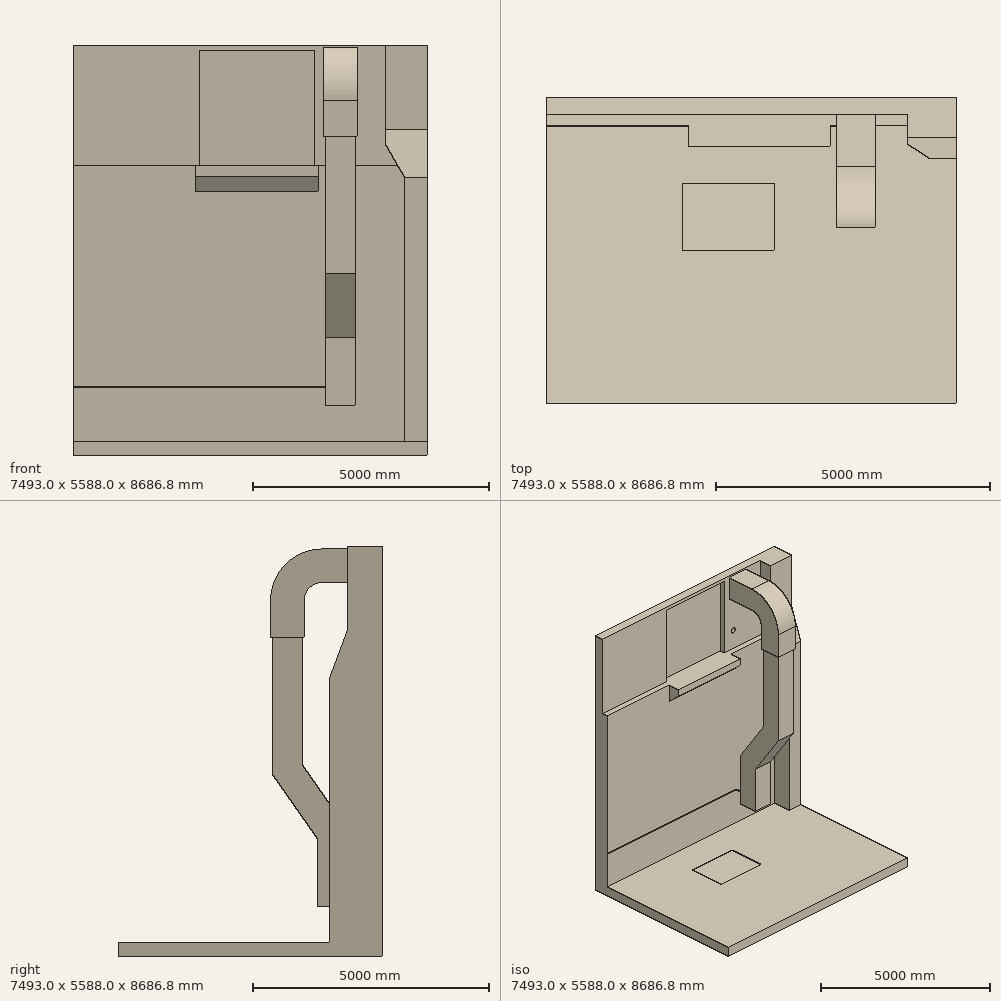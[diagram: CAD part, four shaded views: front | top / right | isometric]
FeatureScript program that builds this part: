
annotation { "Feature Type Name" : "Feature", "Feature Type Description" : "" }
export const myFeature = defineFeature(function(context is Context, id is Id, definition is map)
    precondition{}
    {
        {
            var Q0;
            Q0=qCreatedBy(makeId("Front.planeOp"),FACE);
            var sketch = newSketch(context, id + "F0", { "sketchPlane" : qUnion([Q0])});
            skLineSegment(sketch, "E0", {"start": v(0, 0) * mm, "end": v(0, 6146.8) * mm});
            skLineSegment(sketch, "E1", {"start": v(0, 6146.8) * mm, "end": v(7493, 6146.8) * mm});
            skLineSegment(sketch, "E2", {"start": v(7493, 6146.8) * mm, "end": v(7493, 0) * mm});
            skLineSegment(sketch, "E3", {"start": v(7493, 0) * mm, "end": v(0, 0) * mm});
            skSolve(sketch);
        }
        {
            var Q0;
            Q0=makeQuery(id+"F0.imprint","IMPRINT",FACE,{"disambiguationData":[TD([[makeQuery(id+"F0.imprint","IMPRINT",EDGE,{"derivedFrom":sQuery(id+"F0.wireOp",EDGE,"E0")}),-1.0]])]});
            extrude(context, id + "F1", {"entities" : qUnion([Q0]), "depth" : 508 * mm});
        }
        {
            var Q0;
            Q0=makeQuery(id+"F1.opExtrude","CAP_FACE",FACE,{"disambiguationData":[OSD([sQuery(id+"F0.wireOp",EDGE,"E0"),sQuery(id+"F0.wireOp",EDGE,"E1"),sQuery(id+"F0.wireOp",EDGE,"E2"),sQuery(id+"F0.wireOp",EDGE,"E3")])],"isStart":false});
            var sketch = newSketch(context, id + "F2", { "sketchPlane" : qUnion([Q0])});
            skLineSegment(sketch, "E4.bottom", {"start": v(0, 0) * mm, "end": v(7493, 0) * mm});
            skLineSegment(sketch, "E4.top", {"start": v(0, 304.8) * mm, "end": v(7493, 304.8) * mm});
            skLineSegment(sketch, "E4.left", {"start": v(0, 0) * mm, "end": v(0, 304.8) * mm});
            skLineSegment(sketch, "E4.right", {"start": v(7493, 0) * mm, "end": v(7493, 304.8) * mm});
            skSolve(sketch);
        }
        {
            var Q0;
            Q0=makeQuery(id+"F2.imprint","IMPRINT",FACE,{"disambiguationData":[TD([[makeQuery(id+"F2.imprint","IMPRINT",EDGE,{"derivedFrom":sQuery(id+"F2.wireOp",EDGE,"E4.bottom")}),-1.0]])]});
            extrude(context, id + "F3", {"entities" : qUnion([Q0]), "operationType" : NewBodyOperationType.ADD, "depth" : 5080 * mm});
        }
        {
            var Q0;
            Q0=makeQuery(id+"F1.opExtrude","SWEPT_FACE",FACE,{"disambiguationData":[OSD([sQuery(id+"F0.wireOp",EDGE,"E1")])]});
            var sketch = newSketch(context, id + "F4", { "sketchPlane" : qUnion([Q0])});
            skLineSegment(sketch, "E5.bottom", {"start": v(0, 0) * mm, "end": v(7493, 0) * mm});
            skLineSegment(sketch, "E5.top", {"start": v(0, -304.8) * mm, "end": v(7493, -304.8) * mm});
            skLineSegment(sketch, "E5.left", {"start": v(0, 0) * mm, "end": v(0, -304.8) * mm});
            skLineSegment(sketch, "E5.right", {"start": v(7493, 0) * mm, "end": v(7493, -304.8) * mm});
            skSolve(sketch);
        }
        {
            var Q0;
            Q0=makeQuery(id+"F4.imprint","IMPRINT",FACE,{"disambiguationData":[TD([[makeQuery(id+"F4.imprint","IMPRINT",EDGE,{"derivedFrom":sQuery(id+"F4.wireOp",EDGE,"E5.bottom")}),-1.0]])]});
            extrude(context, id + "F5", {"entities" : qUnion([Q0]), "operationType" : NewBodyOperationType.ADD, "depth" : 2540 * mm});
        }
        {
            var Q0;
            Q0=makeQuery(id+"F1.opExtrude","CAP_FACE",FACE,{"disambiguationData":[OSD([sQuery(id+"F0.wireOp",EDGE,"E0"),sQuery(id+"F0.wireOp",EDGE,"E1"),sQuery(id+"F0.wireOp",EDGE,"E2"),sQuery(id+"F0.wireOp",EDGE,"E3")])],"isStart":false});
            var sketch = newSketch(context, id + "F6", { "sketchPlane" : qUnion([Q0])});
            skLineSegment(sketch, "E6", {"start": v(7493, 304.8) * mm, "end": v(7010.4, 304.8) * mm});
            skLineSegment(sketch, "E7", {"start": v(6604, 8686.8) * mm, "end": v(7493, 8686.8) * mm});
            skLineSegment(sketch, "E8", {"start": v(7493, 8686.8) * mm, "end": v(7493, 304.8) * mm});
            skLineSegment(sketch, "E9", {"start": v(7010.4, 304.8) * mm, "end": v(7010.4, 5892.8) * mm});
            skLineSegment(sketch, "E10", {"start": v(7010.4, 5892.8) * mm, "end": v(6604, 6596.7) * mm});
            skLineSegment(sketch, "E11", {"start": v(6604, 6596.7) * mm, "end": v(6604, 8686.8) * mm});
            skSolve(sketch);
        }
        {
            var Q0;
            Q0 = qSketchRegion(id + "F6", true);
            var Q1;
            Q1=makeQuery(id+"F5.opExtrude","SWEPT_FACE",FACE,{"disambiguationData":[OSD([sQuery(id+"F4.wireOp",EDGE,"E5.top")])]});
            extrude(context, id + "F7", {"entities" : qUnion([Q0]), "operationType" : NewBodyOperationType.ADD, "depth" : 609.6 * mm, "hasSecondDirection" : true, "secondDirectionBound" : SecondDirectionBoundingType.UP_TO_SURFACE, "secondDirectionOppositeDirection" : true, "secondDirectionBoundEntityFace" : qUnion([Q1]), "secondDirectionDepth" : 25.4 * mm});
        }
        {
            var Q0;
            Q0=makeQuery(id+"F1.opExtrude","CAP_FACE",FACE,{"disambiguationData":[OSD([sQuery(id+"F0.wireOp",EDGE,"E0"),sQuery(id+"F0.wireOp",EDGE,"E1"),sQuery(id+"F0.wireOp",EDGE,"E2"),sQuery(id+"F0.wireOp",EDGE,"E3")])],"isStart":false});
            var sketch = newSketch(context, id + "F8", { "sketchPlane" : qUnion([Q0])});
            skLineSegment(sketch, "E12", {"start": v(2590.8, 6146.8) * mm, "end": v(2590.8, 5588) * mm});
            skLineSegment(sketch, "E13", {"start": v(2590.8, 5588) * mm, "end": v(5181.6, 5588) * mm});
            skLineSegment(sketch, "E14", {"start": v(5181.6, 5588) * mm, "end": v(5181.6, 6146.8) * mm});
            skLineSegment(sketch, "E15", {"start": v(5181.6, 6146.8) * mm, "end": v(2590.8, 6146.8) * mm});
            skSolve(sketch);
        }
        {
            var Q0;
            Q0=makeQuery(id+"F8.imprint","IMPRINT",FACE,{"disambiguationData":[TD([[makeQuery(id+"F8.imprint","IMPRINT",EDGE,{"derivedFrom":sQuery(id+"F8.wireOp",EDGE,"E12")}),1.0]])]});
            extrude(context, id + "F9", {"entities" : qUnion([Q0]), "operationType" : NewBodyOperationType.ADD, "depth" : 381 * mm});
        }
        {
            var Q0;
            Q0=makeQuery(id+"F9.opExtrude","SWEPT_FACE",FACE,{"disambiguationData":[OSD([sQuery(id+"F8.wireOp",EDGE,"E12")])]});
            var sketch = newSketch(context, id + "F10", { "sketchPlane" : qUnion([Q0])});
            skLineSegment(sketch, "E16", {"start": v(508, 5588) * mm, "end": v(889, 5918.2) * mm});
            skLineSegment(sketch, "E17", {"start": v(889, 5918.2) * mm, "end": v(889, 5588) * mm});
            skLineSegment(sketch, "E18", {"start": v(889, 5588) * mm, "end": v(508, 5588) * mm});
            skSolve(sketch);
        }
        {
            var Q0;
            Q0=makeQuery(id+"F10.imprint","IMPRINT",FACE,{"disambiguationData":[TD([[makeQuery(id+"F10.imprint","IMPRINT",EDGE,{"derivedFrom":sQuery(id+"F10.wireOp",EDGE,"E16")}),-1.0]])]});
            var Q1;
            Q1=makeQuery(id+"F9.opExtrude","SWEPT_FACE",FACE,{"disambiguationData":[OSD([sQuery(id+"F8.wireOp",EDGE,"E14")])]});
            extrude(context, id + "F11", {"entities" : qUnion([Q0]), "operationType" : NewBodyOperationType.REMOVE, "endBound" : BoundingType.UP_TO_SURFACE, "oppositeDirection" : true, "endBoundEntityFace" : qUnion([Q1]), "depth" : 25.4 * mm});
        }
        {
            var Q0;
            Q0=makeQuery(id+"F5.opExtrude","SWEPT_FACE",FACE,{"disambiguationData":[OSD([sQuery(id+"F4.wireOp",EDGE,"E5.top")])]});
            var sketch = newSketch(context, id + "F12", { "sketchPlane" : qUnion([Q0])});
            skLineSegment(sketch, "E19", {"start": v(2667, 6146.8) * mm, "end": v(2667, 8585.2) * mm});
            skLineSegment(sketch, "E20", {"start": v(2667, 8585.2) * mm, "end": v(5105.4, 8585.2) * mm});
            skLineSegment(sketch, "E21", {"start": v(5105.4, 8585.2) * mm, "end": v(5105.4, 6146.8) * mm});
            skLineSegment(sketch, "E22", {"start": v(5105.4, 6146.8) * mm, "end": v(2667, 6146.8) * mm});
            skSolve(sketch);
        }
        {
            var Q0;
            Q0=makeQuery(id+"F12.imprint","IMPRINT",FACE,{"disambiguationData":[TD([[makeQuery(id+"F12.imprint","IMPRINT",EDGE,{"derivedFrom":sQuery(id+"F12.wireOp",EDGE,"E19")}),-1.0]])]});
            extrude(context, id + "F13", {"entities" : qUnion([Q0]), "operationType" : NewBodyOperationType.REMOVE, "oppositeDirection" : true, "depth" : 152.4 * mm});
        }
        {
            var Q0;
            Q0=makeQuery(id+"F7.opExtrude","SWEPT_FACE",FACE,{"disambiguationData":[OSD([sQuery(id+"F6.wireOp",EDGE,"E11")])]});
            var sketch = newSketch(context, id + "F14", { "sketchPlane" : qUnion([Q0])});
            skLineSegment(sketch, "E23", {"start": v(736.6, 6908.8) * mm, "end": v(1117.6, 5892.8) * mm});
            skLineSegment(sketch, "E24", {"start": v(1117.6, 5892.8) * mm, "end": v(1117.6, 8686.8) * mm});
            skLineSegment(sketch, "E25", {"start": v(736.6, 6908.8) * mm, "end": v(736.6, 8686.8) * mm});
            skPoint(sketch, "E25.endSnap0", {"position": v(711.2, 8686.8) * mm});
            skLineSegment(sketch, "E26", {"start": v(736.6, 8686.8) * mm, "end": v(1117.6, 8686.8) * mm});
            skSolve(sketch);
        }
        {
            var Q0;
            Q0 = qSketchRegion(id + "F14", true);
            var Q1;
            Q1=makeQuery(id+"F7.boolean.opBoolean","MERGE",FACE,{"derivedFrom":[makeQuery(id+"F5.boolean.opBoolean","MERGE",FACE,{"derivedFrom":[makeQuery(id+"F3.boolean.opBoolean","MERGE",FACE,{"derivedFrom":[makeQuery(id+"F1.opExtrude","SWEPT_FACE",FACE,{"disambiguationData":[OSD([sQuery(id+"F0.wireOp",EDGE,"E2")])]}),makeQuery(id+"F3.opExtrude","SWEPT_FACE",FACE,{"disambiguationData":[OSD([sQuery(id+"F2.wireOp",EDGE,"E4.right")])]})]}),makeQuery(id+"F5.opExtrude","SWEPT_FACE",FACE,{"disambiguationData":[OSD([sQuery(id+"F4.wireOp",EDGE,"E5.right")])]})]}),makeQuery(id+"F7.opExtrude","SWEPT_FACE",FACE,{"disambiguationData":[OSD([sQuery(id+"F6.wireOp",EDGE,"E8")])]})]});
            extrude(context, id + "F15", {"entities" : qUnion([Q0]), "operationType" : NewBodyOperationType.REMOVE, "endBound" : BoundingType.UP_TO_SURFACE, "oppositeDirection" : true, "endBoundEntityFace" : qUnion([Q1]), "depth" : 25.4 * mm});
        }
        {
            var Q0;
            Q0=makeQuery(id+"F3.opExtrude","SWEPT_FACE",FACE,{"disambiguationData":[OSD([sQuery(id+"F2.wireOp",EDGE,"E4.top")])]});
            cPlane(context, id + "F16", {"entities" : qUnion([Q0]), "cplaneType" : CPlaneType.OFFSET, "offset" : 762 * mm, "width" : 152.4 * mm, "height" : 152.4 * mm});
        }
        {
            var Q0;
            Q0=qCreatedBy(id+"F16.planeOp",FACE);
            var sketch = newSketch(context, id + "F17", { "sketchPlane" : qUnion([Q0])});
            skLineSegment(sketch, "E27", {"start": v(5334, -736.6) * mm, "end": v(5334, -1371.6) * mm});
            skLineSegment(sketch, "E28", {"start": v(5334, -1371.6) * mm, "end": v(5969, -1371.6) * mm});
            skLineSegment(sketch, "E29", {"start": v(5969, -1371.6) * mm, "end": v(5969, -736.6) * mm});
            skLineSegment(sketch, "E30", {"start": v(5969, -736.6) * mm, "end": v(5334, -736.6) * mm});
            skPoint(sketch, "E31", {"position": v(5651.5, -1054.1) * mm});
            skPoint(sketch, "E31.positionSnap0", {"position": v(5334, -1054.1) * mm});
            skPoint(sketch, "E31.positionSnap1", {"position": v(5651.5, -1371.6) * mm});
            skSolve(sketch);
        }
        {
            var Q0;
            Q0=sQuery(id+"F17.wireOp",VERTEX,"E31");
            var Q1;
            Q1=qCreatedBy(makeId("Right.planeOp"),FACE);
            cPlane(context, id + "F18", {"entities" : qUnion([Q0, Q1]), "cplaneType" : CPlaneType.PLANE_POINT, "offset" : 25.4 * mm, "width" : 152.4 * mm, "height" : 152.4 * mm});
        }
        {
            var Q0;
            Q0=qCreatedBy(id+"F18.planeOp",FACE);
            var sketch = newSketch(context, id + "F19", { "sketchPlane" : qUnion([Q0])});
            skLineSegment(sketch, "E32", {"start": v(-1054.1, 1066.8) * mm, "end": v(-1054.1, 2590.8) * mm});
            skLineSegment(sketch, "E33", {"start": v(-1054.1, 2590.8) * mm, "end": v(-2015.64, 3964.03) * mm});
            skLineSegment(sketch, "E34", {"start": v(-2015.64, 3964.03) * mm, "end": v(-2015.64, 6756.4) * mm});
            skSolve(sketch);
        }
        {
            var Q0;
            Q0=makeQuery(id+"F17.imprint","IMPRINT",FACE,{"disambiguationData":[TD([[makeQuery(id+"F17.imprint","IMPRINT",EDGE,{"derivedFrom":sQuery(id+"F17.wireOp",EDGE,"E27")}),1.0]])]});
            var Q1;
            Q1=sQuery(id+"F19.wireOp",EDGE,"E32");
            var Q2;
            Q2=sQuery(id+"F19.wireOp",EDGE,"E33");
            var Q3;
            Q3=sQuery(id+"F19.wireOp",EDGE,"E34");
            sweep(context, id + "F20", {"profiles" : qUnion([Q0]), "path" : qUnion([Q1, Q2, Q3])});
        }
        {
            var Q0;
            Q0=makeQuery(id+"F20.opSweep","CAP_FACE",FACE,{"disambiguationData":[OSD([sQuery(id+"F17.wireOp",EDGE,"E27"),sQuery(id+"F17.wireOp",EDGE,"E28"),sQuery(id+"F17.wireOp",EDGE,"E29"),sQuery(id+"F17.wireOp",EDGE,"E30"),sQuery(id+"F19.wireOp",VERTEX,"E34.end")])],"isStart":false});
            var sketch = newSketch(context, id + "F21", { "sketchPlane" : qUnion([Q0])});
            skLineSegment(sketch, "E35.bottom", {"start": v(5295.9, -2371.24) * mm, "end": v(6007.1, -2371.24) * mm});
            skLineSegment(sketch, "E35.top", {"start": v(5295.9, -1660.04) * mm, "end": v(6007.1, -1660.04) * mm});
            skLineSegment(sketch, "E35.left", {"start": v(5295.9, -2371.24) * mm, "end": v(5295.9, -1660.04) * mm});
            skLineSegment(sketch, "E35.right", {"start": v(6007.1, -2371.24) * mm, "end": v(6007.1, -1660.04) * mm});
            skPoint(sketch, "E35.middle", {"position": v(5651.5, -2015.64) * mm});
            skPoint(sketch, "E35.middle.positionSnap0", {"position": v(5334, -2015.64) * mm});
            skPoint(sketch, "E35.middle.positionSnap1", {"position": v(5651.5, -1698.14) * mm});
            skPoint(sketch, "E35.centerSnap0", {"position": v(5334, -2015.64) * mm});
            skPoint(sketch, "E35.centerSnap1", {"position": v(5651.5, -1698.14) * mm});
            skSolve(sketch);
        }
        {
            var Q0;
            Q0=qCreatedBy(id+"F18.planeOp",FACE);
            var sketch = newSketch(context, id + "F22", { "sketchPlane" : qUnion([Q0])});
            skLineSegment(sketch, "E36", {"start": v(-2015.64, 6756.4) * mm, "end": v(-2015.64, 7518.4) * mm});
            skArc(sketch, "E37", {"start": v(-1253.64, 8280.4) * mm, "mid": v(-1792.46, 8057.22) * mm, "end": v(-2015.64, 7518.4) * mm});
            skLineSegment(sketch, "E38", {"start": v(-1253.64, 8280.4) * mm, "end": v(-304.8, 8280.4) * mm});
            skSolve(sketch);
        }
        {
            var Q0;
            Q0 = qSketchRegion(id + "F21", true);
            var Q1;
            Q1=sQuery(id+"F22.wireOp",EDGE,"E36");
            var Q2;
            Q2=sQuery(id+"F22.wireOp",EDGE,"E37");
            var Q3;
            Q3=sQuery(id+"F22.wireOp",EDGE,"E38");
            sweep(context, id + "F23", {"profiles" : qUnion([Q0]), "path" : qUnion([Q1, Q2, Q3])});
        }
        {
            var Q0;
            Q0=makeQuery(id+"F5.boolean.opBoolean","MERGE",FACE,{"derivedFrom":[makeQuery(id+"F3.boolean.opBoolean","MERGE",FACE,{"derivedFrom":[makeQuery(id+"F1.opExtrude","SWEPT_FACE",FACE,{"disambiguationData":[OSD([sQuery(id+"F0.wireOp",EDGE,"E0")])]}),makeQuery(id+"F3.opExtrude","SWEPT_FACE",FACE,{"disambiguationData":[OSD([sQuery(id+"F2.wireOp",EDGE,"E4.left")])]})]}),makeQuery(id+"F5.opExtrude","SWEPT_FACE",FACE,{"disambiguationData":[OSD([sQuery(id+"F4.wireOp",EDGE,"E5.left")])]})]});
            var sketch = newSketch(context, id + "F24", { "sketchPlane" : qUnion([Q0])});
            skCircle(sketch, "E39", {"center": v(520.7, 1447.8) * mm, "radius": 12.7 * mm});
            skSolve(sketch);
        }
        {
            var Q0;
            Q0=sQuery(id+"F24.wireOp",VERTEX,"E39.center");
            var Q1;
            Q1=qCreatedBy(makeId("Top.planeOp"),FACE);
            cPlane(context, id + "F25", {"entities" : qUnion([Q0, Q1]), "cplaneType" : CPlaneType.PLANE_POINT, "offset" : 25.4 * mm, "width" : 152.4 * mm, "height" : 152.4 * mm});
        }
        {
            var Q0;
            Q0=qCreatedBy(id+"F25.planeOp",FACE);
            var sketch = newSketch(context, id + "F26", { "sketchPlane" : qUnion([Q0])});
            skLineSegment(sketch, "E40", {"start": v(0, -520.7) * mm, "end": v(5384.8, -520.7) * mm});
            skLineSegment(sketch, "E41", {"start": v(5384.8, -520.7) * mm, "end": v(5384.8, -736.6) * mm});
            skSolve(sketch);
        }
        {
            var Q0;
            Q0=makeQuery(id+"F24.imprint","IMPRINT",FACE,{"disambiguationData":[TD([[makeQuery(id+"F24.imprint","IMPRINT",EDGE,{"derivedFrom":sQuery(id+"F24.wireOp",EDGE,"E39")}),1.0]])]});
            var Q1;
            Q1=sQuery(id+"F26.wireOp",EDGE,"E40");
            var Q2;
            Q2=sQuery(id+"F26.wireOp",EDGE,"E41");
            sweep(context, id + "F27", {"profiles" : qUnion([Q0]), "path" : qUnion([Q1, Q2])});
        }
        {
            var Q0;
            Q0=makeQuery(id+"F1.opExtrude","CAP_FACE",FACE,{"disambiguationData":[OSD([sQuery(id+"F0.wireOp",EDGE,"E0"),sQuery(id+"F0.wireOp",EDGE,"E1"),sQuery(id+"F0.wireOp",EDGE,"E2"),sQuery(id+"F0.wireOp",EDGE,"E3")])],"isStart":false});
            cPlane(context, id + "F28", {"entities" : qUnion([Q0]), "cplaneType" : CPlaneType.OFFSET, "offset" : 152.4 * mm, "width" : 152.4 * mm, "height" : 152.4 * mm});
        }
        {
            var Q0;
            Q0=makeQuery(id+"F3.opExtrude","SWEPT_FACE",FACE,{"disambiguationData":[OSD([sQuery(id+"F2.wireOp",EDGE,"E4.top")])]});
            var sketch = newSketch(context, id + "F29", { "sketchPlane" : qUnion([Q0])});
            skLineSegment(sketch, "E42", {"start": v(2482.94, -1574.8) * mm, "end": v(4169.99, -1574.8) * mm});
            skLineSegment(sketch, "E43", {"start": v(4169.99, -1574.8) * mm, "end": v(4169.99, -2799.17) * mm});
            skLineSegment(sketch, "E44", {"start": v(4169.99, -2799.17) * mm, "end": v(2482.94, -2799.17) * mm});
            skLineSegment(sketch, "E45", {"start": v(2482.94, -2799.17) * mm, "end": v(2482.94, -1574.8) * mm});
            skSolve(sketch);
        }
        {
            var Q0;
            Q0=makeQuery(id+"F29.imprint","IMPRINT",FACE,{"disambiguationData":[TD([[makeQuery(id+"F29.imprint","IMPRINT",EDGE,{"derivedFrom":sQuery(id+"F29.wireOp",EDGE,"E42")}),-1.0]])]});
            extrude(context, id + "F30", {"entities" : qUnion([Q0]), "operationType" : NewBodyOperationType.REMOVE, "oppositeDirection" : true, "depth" : 25.4 * mm});
        }
        {
            var Q0;
            Q0=makeQuery(id+"F5.boolean.opBoolean","MERGE",FACE,{"derivedFrom":[makeQuery(id+"F1.opExtrude","CAP_FACE",FACE,{"disambiguationData":[OSD([sQuery(id+"F0.wireOp",EDGE,"E0"),sQuery(id+"F0.wireOp",EDGE,"E1"),sQuery(id+"F0.wireOp",EDGE,"E2"),sQuery(id+"F0.wireOp",EDGE,"E3")])],"isStart":true}),makeQuery(id+"F5.opExtrude","SWEPT_FACE",FACE,{"disambiguationData":[OSD([sQuery(id+"F4.wireOp",EDGE,"E5.bottom")])]})]});
            var sketch = newSketch(context, id + "F31", { "sketchPlane" : qUnion([Q0])});
            skCircle(sketch, "E46", {"center": v(-5486.4, 6756.4) * mm, "radius": 84.14 * mm});
            skSolve(sketch);
        }
        {
            var Q0;
            Q0 = qSketchRegion(id + "F31", true);
            var Q1;
            Q1=makeQuery(id+"F5.opExtrude","SWEPT_FACE",FACE,{"disambiguationData":[OSD([sQuery(id+"F4.wireOp",EDGE,"E5.top")])]});
            extrude(context, id + "F32", {"entities" : qUnion([Q0]), "operationType" : NewBodyOperationType.REMOVE, "endBound" : BoundingType.UP_TO_SURFACE, "oppositeDirection" : true, "endBoundEntityFace" : qUnion([Q1]), "depth" : 25.4 * mm});
        }
    });
